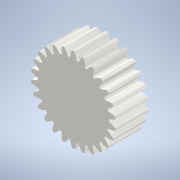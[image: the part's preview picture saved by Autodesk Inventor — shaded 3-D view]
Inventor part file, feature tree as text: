
AUTODESK INVENTOR PART (.ipt)
format: ipt  version: 2022 (Build 260153000, 153)  size: 244,736 bytes
history: native  units: mm (DEFAULTED — no unit token found)
features: plane x3, other x3, sketch x2, extrude x1
ambient origin geometry x8: Origin, YZ Plane, XZ Plane, XY Plane, X Axis, Y Axis, Z Axis, Center Point
bodies: Solid1 (feature_tree)
feature tree (9):
  extrude  "Extrusion1"  Depth=5.0mm TaperAngle=0.0deg
  plane  "Work Plane2"
  plane  "Work Plane8"
  plane  "Work Plane9"
  other  "Spur Gear"
  sketch  "Sketch1"  dims[d0=12.596515mm d1=5.0mm d2=0.0mm]
  sketch  "Sketch2"  dims[d3=11.7mm d4=10.0mm d5=0.0mm d16=12.0mm d17=0.0mm d34=1.208305mm d39=0.0mm d41=0.0mm d43=12.0mm d46=12.0mm d47=0.0mm d48=0.0mm]
  other  "Srf1"
  other  "Pitch Diameter"
